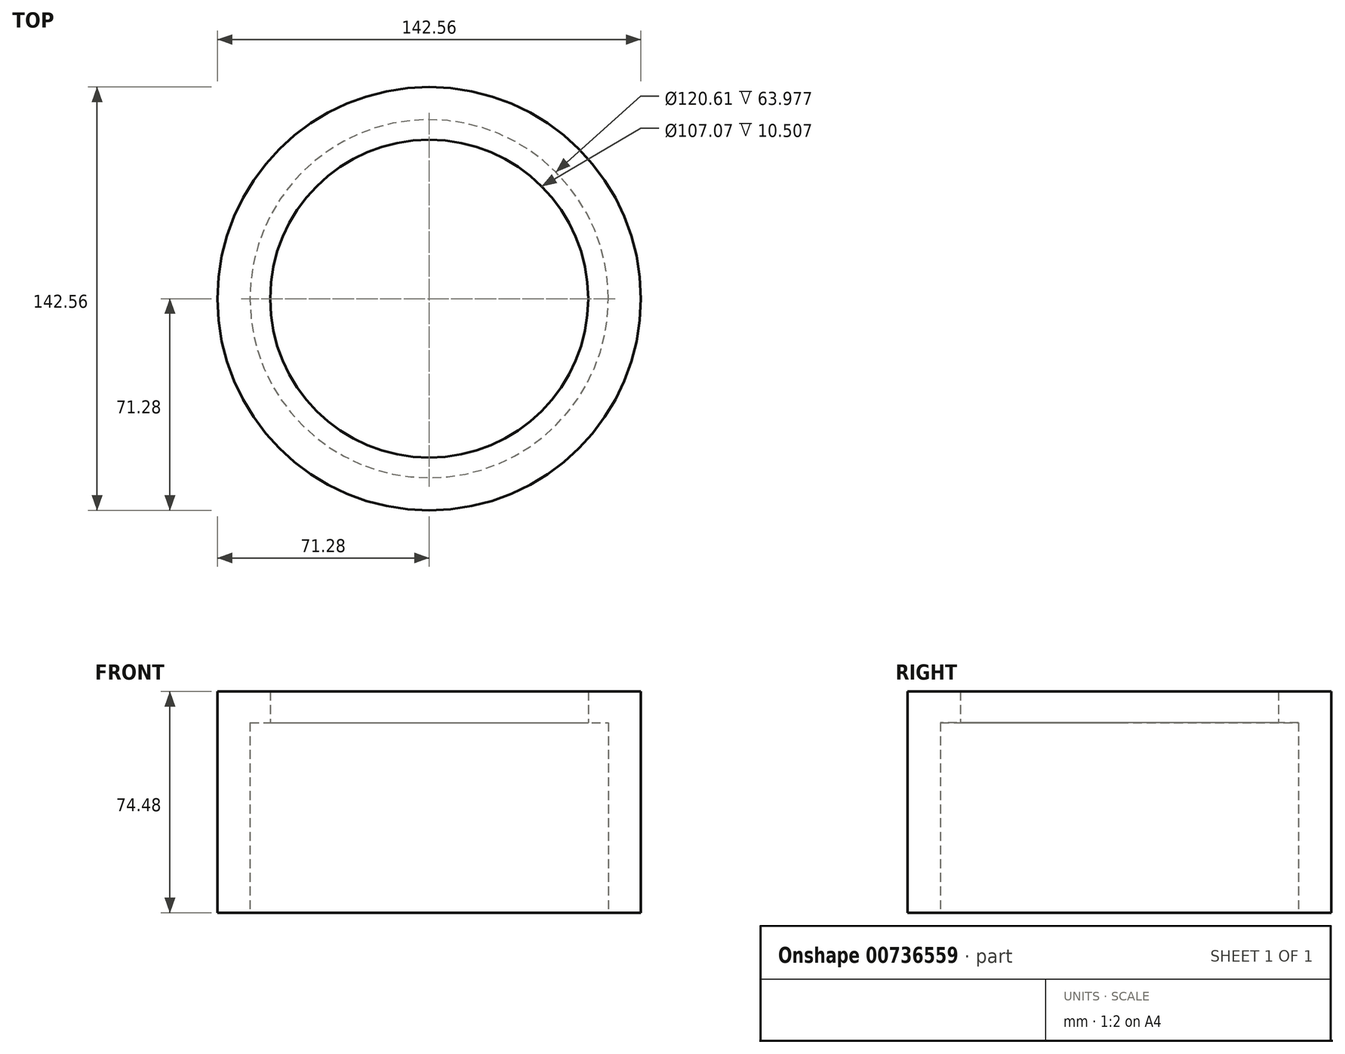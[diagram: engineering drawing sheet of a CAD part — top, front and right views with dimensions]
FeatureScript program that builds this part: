
annotation { "Feature Type Name" : "Feature", "Feature Type Description" : "" }
export const myFeature = defineFeature(function(context is Context, id is Id, definition is map)
    precondition{}
    {
        {
            var Q0;
            Q0=qCreatedBy(makeId("Front.planeOp"),FACE);
            var sketch = newSketch(context, id + "F0", { "sketchPlane" : qUnion([Q0])});
            skLineSegment(sketch, "E0", {"start": v(-71.28, 20.9) * mm, "end": v(-71.28, -53.58) * mm});
            skLineSegment(sketch, "E1", {"start": v(-71.28, -53.58) * mm, "end": v(-60.3, -53.58) * mm});
            skLineSegment(sketch, "E2", {"start": v(-60.3, -53.58) * mm, "end": v(-60.3, 10.4) * mm});
            skLineSegment(sketch, "E3", {"start": v(-60.3, 10.4) * mm, "end": v(-53.53, 10.4) * mm});
            skLineSegment(sketch, "E4", {"start": v(-53.53, 10.4) * mm, "end": v(-53.53, 20.9) * mm});
            skLineSegment(sketch, "E5", {"start": v(-53.53, 20.9) * mm, "end": v(-71.28, 20.9) * mm});
            skLineSegment(sketch, "E6", {"start": v(0, 0) * mm, "end": v(0, 23.94) * mm});
            skSolve(sketch);
        }
        {
            var Q0;
            Q0=makeQuery(id+"F0.imprint","IMPRINT",FACE,{"disambiguationData":[TD([[makeQuery(id+"F0.imprint","IMPRINT",EDGE,{"derivedFrom":sQuery(id+"F0.wireOp",EDGE,"E0")}),1.0]])]});
            var Q1;
            Q1=sQuery(id+"F0.wireOp",EDGE,"E6");
            revolve(context, id + "F1", {"surfaceOperationType" : NewSurfaceOperationType.NEW, "entities" : qUnion([Q0]), "axis" : qUnion([Q1]), "revolveType" : RevolveType.FULL});
        }
        {
            var Q0;
            Q0=qCreatedBy(makeId("Front.planeOp"),FACE);
            cPlane(context, id + "F2", {"entities" : qUnion([Q0]), "cplaneType" : CPlaneType.OFFSET, "offset" : 78.23 * mm, "width" : 152.4 * mm, "height" : 152.4 * mm});
        }
    });
